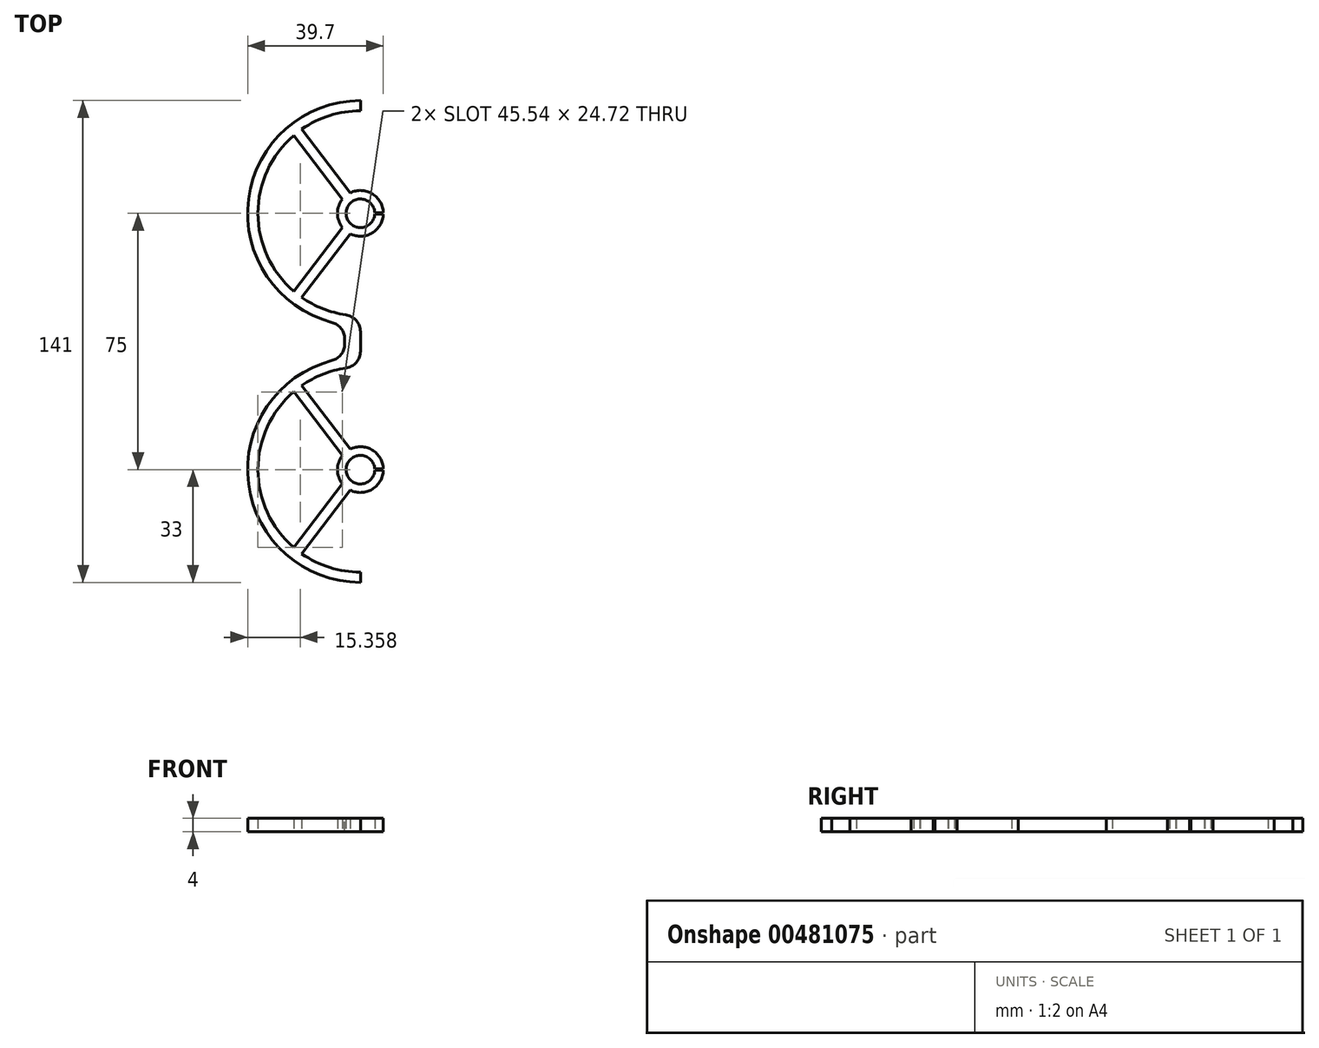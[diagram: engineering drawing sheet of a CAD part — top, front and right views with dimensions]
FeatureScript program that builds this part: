
annotation { "Feature Type Name" : "Feature", "Feature Type Description" : "" }
export const myFeature = defineFeature(function(context is Context, id is Id, definition is map)
    precondition{}
    {
        {
            var Q0;
            Q0=qCreatedBy(makeId("Top.planeOp"),FACE);
            var sketch = newSketch(context, id + "F0", { "sketchPlane" : qUnion([Q0])});
            skPoint(sketch, "E0", {"position": v(0, 37.5) * mm});
            skPoint(sketch, "E1.MirrorP", {"position": v(0, -37.5) * mm});
            skCircle(sketch, "E2", {"center": v(0, 37.5) * mm, "radius": 4.2 * mm});
            skCircle(sketch, "E3", {"center": v(0, 37.5) * mm, "radius": 6.7 * mm});
            skCircle(sketch, "E4", {"center": v(0, 37.5) * mm, "radius": 30 * mm});
            skLineSegment(sketch, "E5", {"start": v(0, 37.5) * mm, "end": v(45.61, 37.5) * mm, "construction": true});
            skCircle(sketch, "E6", {"center": v(0, 37.5) * mm, "radius": 33 * mm});
            skLineSegment(sketch, "E7", {"start": v(0, 70.5) * mm, "end": v(0, 67.5) * mm});
            skLineSegment(sketch, "E8", {"start": v(0, 7.5) * mm, "end": v(0, 4.5) * mm});
            skLineSegment(sketch, "E9", {"start": v(-17.16, 62.1) * mm, "end": v(-2.96, 43.51) * mm});
            skLineSegment(sketch, "E10", {"start": v(-19.53, 60.27) * mm, "end": v(-5.28, 41.62) * mm});
            skLineSegment(sketch, "E11", {"start": v(0, 37.5) * mm, "end": v(-46.13, 37.5) * mm, "construction": true});
            skLineSegment(sketch, "E12.MirrorCS", {"start": v(-19.53, 14.73) * mm, "end": v(-5.28, 33.38) * mm});
            skLineSegment(sketch, "E13.MirrorCS", {"start": v(-17.16, 12.9) * mm, "end": v(-2.96, 31.49) * mm});
            skLineSegment(sketch, "E14.bottom", {"start": v(-4.6, 4.82) * mm, "end": v(0, 4.82) * mm});
            skLineSegment(sketch, "E14.top", {"start": v(-4.6, 0) * mm, "end": v(0, 0) * mm});
            skLineSegment(sketch, "E14.left", {"start": v(-4.6, 4.82) * mm, "end": v(-4.6, 0) * mm});
            skLineSegment(sketch, "E14.right", {"start": v(0, 4.82) * mm, "end": v(0, 0) * mm});
            skLineSegment(sketch, "E15.bottom", {"start": v(4.2, 37.7) * mm, "end": v(6.7, 37.7) * mm});
            skLineSegment(sketch, "E15.top", {"start": v(4.2, 37.3) * mm, "end": v(6.7, 37.3) * mm});
            skLineSegment(sketch, "E15.left", {"start": v(4.2, 37.7) * mm, "end": v(4.2, 37.3) * mm});
            skLineSegment(sketch, "E15.right", {"start": v(6.7, 37.7) * mm, "end": v(6.7, 37.3) * mm});
            skSolve(sketch);
        }
        {
            var Q0;
            {var subQ0=sQuery(id+"F0.wireOp",EDGE,"E9");Q0=makeQuery(id+"F0.imprint","IMPRINT",FACE,{"disambiguationData":[TD([[makeQuery(id+"F0.imprint","IMPRINT",EDGE,{"derivedFrom":subQ0}),-1.0]])]});}
            var Q1;
            {var subQ5=sQuery(id+"F0.wireOp",EDGE,"E7");Q1=makeQuery(id+"F0.imprint","IMPRINT",FACE,{"disambiguationData":[TD([[makeQuery(id+"F0.imprint","IMPRINT",EDGE,{"derivedFrom":subQ5}),-1.0]])]});}
            var Q2;
            {var subQ0=sQuery(id+"F0.wireOp",EDGE,"E12.MirrorCS");Q2=makeQuery(id+"F0.imprint","IMPRINT",FACE,{"disambiguationData":[TD([[makeQuery(id+"F0.imprint","IMPRINT",EDGE,{"derivedFrom":subQ0}),-1.0]])]});}
            var Q3;
            {var subQ4=sQuery(id+"F0.wireOp",EDGE,"E14.top");Q3=makeQuery(id+"F0.imprint","IMPRINT",FACE,{"disambiguationData":[TD([[makeQuery(id+"F0.imprint","IMPRINT",EDGE,{"derivedFrom":subQ4}),1.0]])]});}
            var Q4;
            {var subQ0=sQuery(id+"F0.wireOp",EDGE,"E14.bottom");Q4=makeQuery(id+"F0.imprint","IMPRINT",FACE,{"disambiguationData":[TD([[makeQuery(id+"F0.imprint","IMPRINT",EDGE,{"derivedFrom":subQ0}),-1.0]])]});}
            var Q5;
            {var subQ5=sQuery(id+"F0.wireOp",EDGE,"E15.bottom");Q5=makeQuery(id+"F0.imprint","IMPRINT",FACE,{"disambiguationData":[TD([[makeQuery(id+"F0.imprint","IMPRINT",EDGE,{"derivedFrom":subQ5}),1.0]])]});}
            extrude(context, id + "F1", {"entities" : qUnion([Q0, Q1, Q2, Q3, Q4, Q5]), "depth" : 4 * mm});
        }
        {
            var Q0;
            Q0=makeQuery(id+"F1.opExtrude","SWEPT_BODY",BODY,{"disambiguationData":[OSD([sQuery(id+"F0.wireOp",EDGE,"E2"),sQuery(id+"F0.wireOp",EDGE,"E3"),sQuery(id+"F0.wireOp",EDGE,"E4"),sQuery(id+"F0.wireOp",EDGE,"E6"),sQuery(id+"F0.wireOp",EDGE,"E7"),sQuery(id+"F0.wireOp",EDGE,"E8"),sQuery(id+"F0.wireOp",EDGE,"E9"),sQuery(id+"F0.wireOp",EDGE,"E10"),sQuery(id+"F0.wireOp",EDGE,"E12.MirrorCS"),sQuery(id+"F0.wireOp",EDGE,"E13.MirrorCS"),sQuery(id+"F0.wireOp",EDGE,"E14.top"),sQuery(id+"F0.wireOp",EDGE,"E14.left"),sQuery(id+"F0.wireOp",EDGE,"E14.right")])]});
            var Q1;
            Q1=qCreatedBy(makeId("Front.planeOp"),FACE);
            mirror(context, id + "F2", {"operationType" : NewBodyOperationType.ADD, "entities" : qUnion([Q0]), "mirrorPlane" : qUnion([Q1])});
        }
        {
            var Q0;
            Q0=makeQuery(id+"F1.opExtrude","SWEPT_EDGE",EDGE,{"disambiguationData":[OSD([sQuery(id+"F0.wireOp",EDGE,"E4"),sQuery(id+"F0.wireOp",EDGE,"E8")])]});
            var Q1;
            Q1=makeQuery(id+"F2.opPattern","COPY",EDGE,{"derivedFrom":makeQuery(id+"F1.opExtrude","SWEPT_EDGE",EDGE,{"disambiguationData":[OSD([sQuery(id+"F0.wireOp",EDGE,"E6"),sQuery(id+"F0.wireOp",EDGE,"E14.bottom"),sQuery(id+"F0.wireOp",EDGE,"E14.left")])]}),"instanceName":"1"});
            var Q2;
            Q2=makeQuery(id+"F1.opExtrude","SWEPT_EDGE",EDGE,{"disambiguationData":[OSD([sQuery(id+"F0.wireOp",EDGE,"E6"),sQuery(id+"F0.wireOp",EDGE,"E14.bottom"),sQuery(id+"F0.wireOp",EDGE,"E14.left")])]});
            var Q3;
            Q3=makeQuery(id+"F2.opPattern","COPY",EDGE,{"derivedFrom":makeQuery(id+"F1.opExtrude","SWEPT_EDGE",EDGE,{"disambiguationData":[OSD([sQuery(id+"F0.wireOp",EDGE,"E4"),sQuery(id+"F0.wireOp",EDGE,"E8")])]}),"instanceName":"1"});
            fillet(context, id + "F3", {"entities" : qUnion([Q0, Q1, Q2, Q3]), "radius" : 5 * mm, "tangentPropagation" : true, "allowEdgeOverflow" : false});
        }
    });
